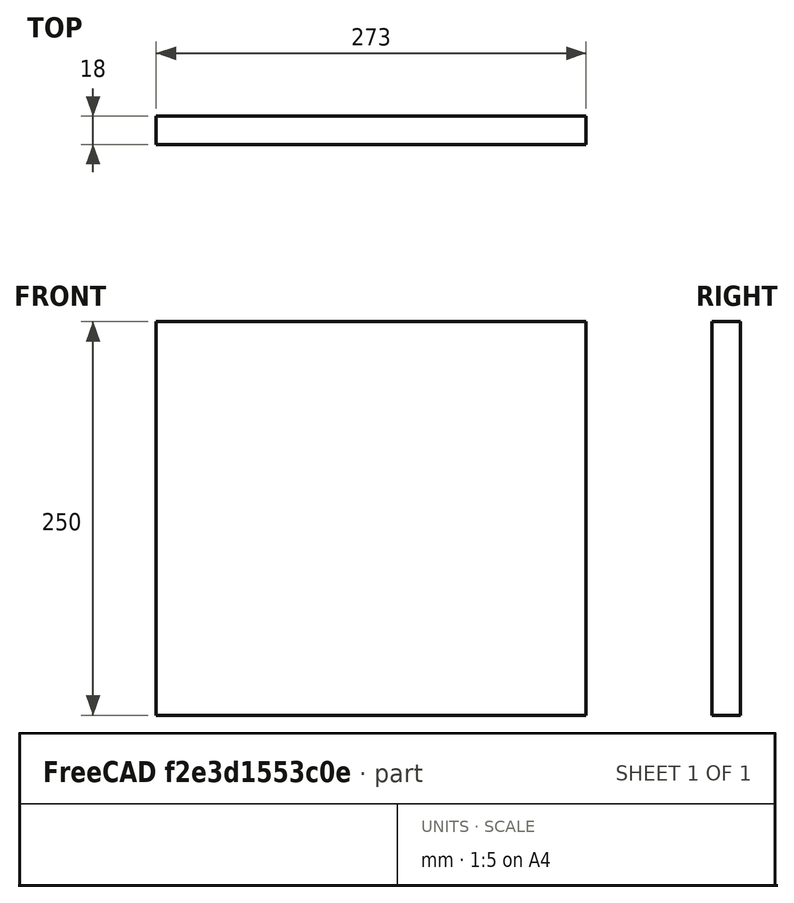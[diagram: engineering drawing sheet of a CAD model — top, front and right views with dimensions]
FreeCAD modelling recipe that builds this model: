
FCSTD DOCUMENT  (FreeCAD 0.18R4 (GitTag))
Label: small_middle
License: All rights reserved
LicenseURL: http://en.wikipedia.org/wiki/All_rights_reserved
objects: Sketcher::SketchObject×1, PartDesign::Pad×1, PartDesign::Body×1
note: 4 computed .brp shape members not serialized (recipe doc carries the construction recipe); baked Part::Feature solids carry a one-line shape summary decoded from their .brp

FEATURE [Sketcher::SketchObject] Sketch
  MapMode = 5
  Placement = pos=(0,0,0) rot=(1,0,0;1.5708rad)
  Support = -> [XZ_Plane]
  sketch-geometry (4):
    g0: LineSegment StartX=0 StartY=0 StartZ=0 EndX=-273 EndY=0 EndZ=0
    g1: LineSegment StartX=-273 StartY=0 StartZ=0 EndX=-273 EndY=250 EndZ=0
    g2: LineSegment StartX=-273 StartY=250 StartZ=0 EndX=0 EndY=250 EndZ=0
    g3: LineSegment StartX=0 StartY=250 StartZ=0 EndX=0 EndY=0 EndZ=0
  constraints (11):
    c: Coincident(g0,g1)
    c: Coincident(g1,g2)
    c: Coincident(g2,g3)
    c: Coincident(g3,g0)
    c: Horizontal(g0)
    c: Horizontal(g2)
    c: Vertical(g1)
    c: Vertical(g3)
    c: Coincident(g0,g-1)
    c: DistanceY(g3,g3) = 250
    c: DistanceX(g0,g0) = 273
FEATURE [PartDesign::Pad] Pad
  Length = 18
  Length2 = 100
  Placement = pos=(0,0,0) rot=(1,0,0;1.5708rad)
  Profile = -> Sketch
  Type = 0
FEATURE [PartDesign::Body] Body
  Group = -> [Sketch,Pad]
  Origin = -> Origin
  Tip = -> Pad
